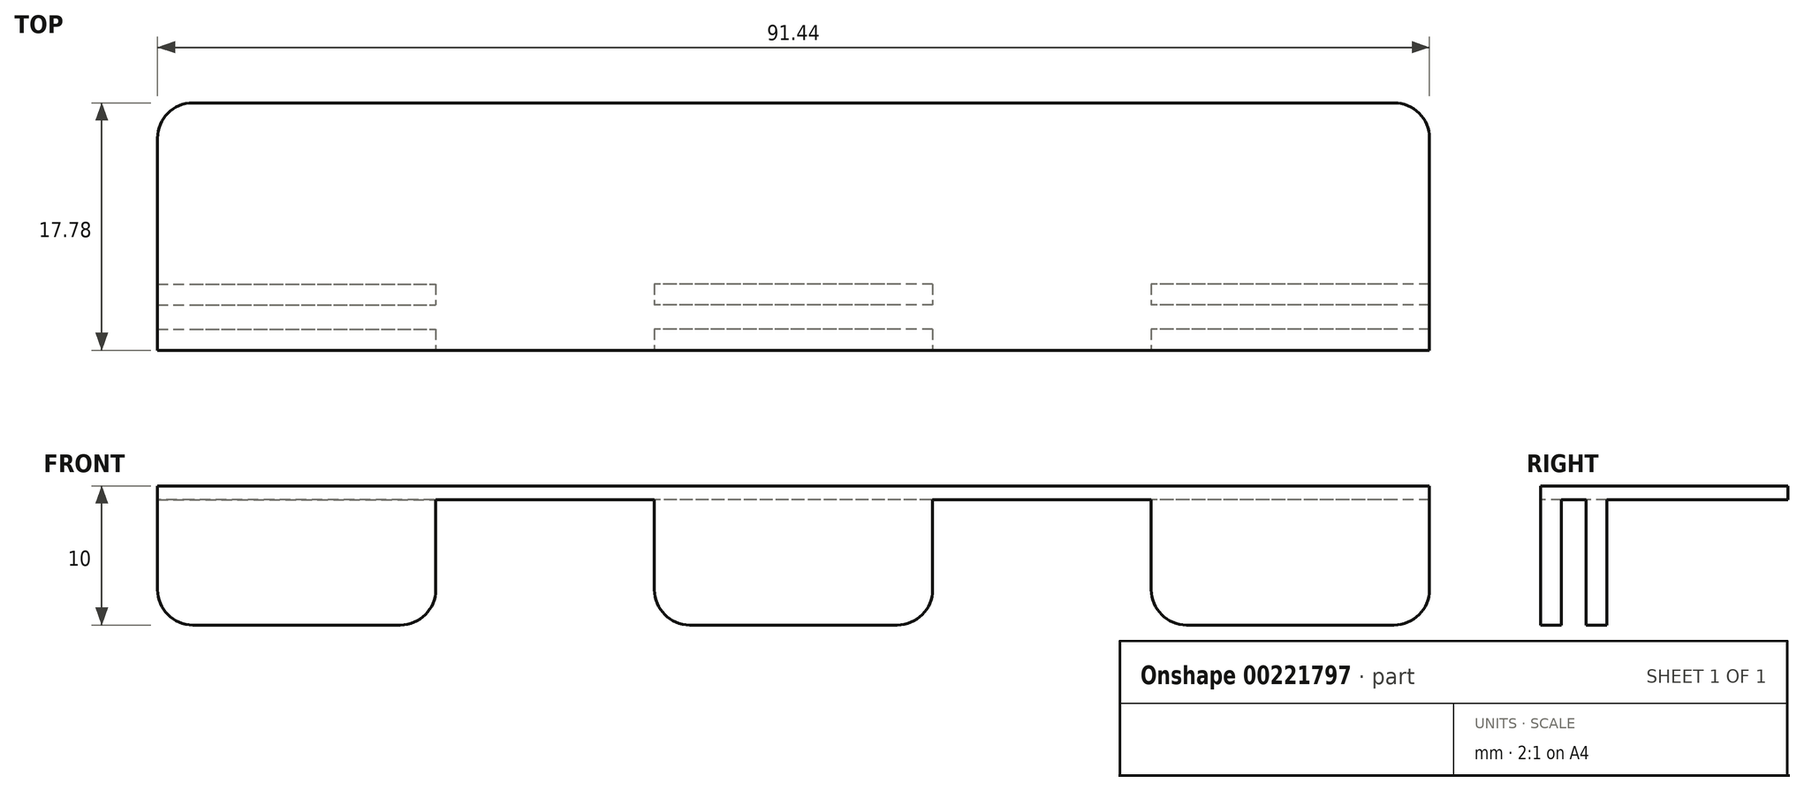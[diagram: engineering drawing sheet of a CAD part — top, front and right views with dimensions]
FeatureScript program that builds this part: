
annotation { "Feature Type Name" : "Feature", "Feature Type Description" : "" }
export const myFeature = defineFeature(function(context is Context, id is Id, definition is map)
    precondition{}
    {
        {
            var Q0;
            Q0=qCreatedBy(makeId("Top.planeOp"),FACE);
            var sketch = newSketch(context, id + "F0", { "sketchPlane" : qUnion([Q0])});
            skLineSegment(sketch, "E0", {"start": v(0, 0) * mm, "end": v(45.72, 0) * mm});
            skLineSegment(sketch, "E1", {"start": v(45.72, 0) * mm, "end": v(45.72, 17.78) * mm});
            skLineSegment(sketch, "E2", {"start": v(45.72, 17.78) * mm, "end": v(0, 17.78) * mm});
            skLineSegment(sketch, "E3", {"start": v(45.72, 3.25) * mm, "end": v(0, 3.25) * mm});
            skLineSegment(sketch, "E4", {"start": v(45.72, 4.75) * mm, "end": v(0, 4.75) * mm});
            skLineSegment(sketch, "E5", {"start": v(45.72, 1.5) * mm, "end": v(0, 1.5) * mm});
            skLineSegment(sketch, "E6.MirrorCS", {"start": v(-45.72, 17.78) * mm, "end": v(0, 17.78) * mm});
            skLineSegment(sketch, "E7.MirrorCS", {"start": v(-45.72, 4.75) * mm, "end": v(0, 4.75) * mm});
            skLineSegment(sketch, "E8.MirrorCS", {"start": v(-45.72, 3.25) * mm, "end": v(0, 3.25) * mm});
            skLineSegment(sketch, "E9.MirrorCS", {"start": v(-45.72, 1.5) * mm, "end": v(0, 1.5) * mm});
            skLineSegment(sketch, "E10.MirrorCS", {"start": v(0, 0) * mm, "end": v(-45.72, 0) * mm});
            skLineSegment(sketch, "E11.MirrorCS", {"start": v(-45.72, 0) * mm, "end": v(-45.72, 17.78) * mm});
            skLineSegment(sketch, "E12", {"start": v(25.72, 4.75) * mm, "end": v(25.72, 3.25) * mm});
            skLineSegment(sketch, "E13", {"start": v(25.72, 1.5) * mm, "end": v(25.72, 0) * mm});
            skLineSegment(sketch, "E14.MirrorCS", {"start": v(-25.72, 4.75) * mm, "end": v(-25.72, 3.25) * mm});
            skLineSegment(sketch, "E15.MirrorCS", {"start": v(-25.72, 1.5) * mm, "end": v(-25.72, 0) * mm});
            skLineSegment(sketch, "E16", {"start": v(10, 4.75) * mm, "end": v(10, 3.25) * mm});
            skLineSegment(sketch, "E17", {"start": v(10, 1.5) * mm, "end": v(10, 0) * mm});
            skLineSegment(sketch, "E18.MirrorCS", {"start": v(-10, 4.75) * mm, "end": v(-10, 3.25) * mm});
            skLineSegment(sketch, "E19.MirrorCS", {"start": v(-10, 1.5) * mm, "end": v(-10, 0) * mm});
            skSolve(sketch);
        }
        {
            var Q0;
            {var subQ1=sQuery(id+"F0.wireOp",EDGE,"E2");Q0=makeQuery(id+"F0.imprint","IMPRINT",FACE,{"disambiguationData":[TD([[makeQuery(id+"F0.imprint","IMPRINT",EDGE,{"derivedFrom":subQ1}),1.0]])]});}
            var Q1;
            {var subQ2=sQuery(id+"F0.wireOp",EDGE,"E3");Q1=makeQuery(id+"F0.imprint","IMPRINT",FACE,{"disambiguationData":[TD([[makeQuery(id+"F0.imprint","IMPRINT",EDGE,{"derivedFrom":subQ2}),-1.0]])]});}
            var Q2;
            {var subQ2=sQuery(id+"F0.wireOp",EDGE,"E3");Q2=makeQuery(id+"F0.imprint","IMPRINT",FACE,{"disambiguationData":[TD([[makeQuery(id+"F0.imprint","IMPRINT",EDGE,{"derivedFrom":subQ2}),1.0]])]});}
            var Q3;
            {var subQ2=sQuery(id+"F0.wireOp",EDGE,"E0");Q3=makeQuery(id+"F0.imprint","IMPRINT",FACE,{"disambiguationData":[TD([[makeQuery(id+"F0.imprint","IMPRINT",EDGE,{"derivedFrom":subQ2}),1.0]])]});}
            var Q4;
            {var subQ3=sQuery(id+"F0.wireOp",EDGE,"E14.MirrorCS");Q4=makeQuery(id+"F0.imprint","IMPRINT",FACE,{"disambiguationData":[TD([[makeQuery(id+"F0.imprint","IMPRINT",EDGE,{"derivedFrom":subQ3}),-1.0]])]});}
            var Q5;
            {var subQ3=sQuery(id+"F0.wireOp",EDGE,"E15.MirrorCS");Q5=makeQuery(id+"F0.imprint","IMPRINT",FACE,{"disambiguationData":[TD([[makeQuery(id+"F0.imprint","IMPRINT",EDGE,{"derivedFrom":subQ3}),-1.0]])]});}
            var Q6;
            {var subQ7=sQuery(id+"F0.wireOp",EDGE,"E12");Q6=makeQuery(id+"F0.imprint","IMPRINT",FACE,{"disambiguationData":[TD([[makeQuery(id+"F0.imprint","IMPRINT",EDGE,{"derivedFrom":subQ7}),-1.0]])]});}
            var Q7;
            {var subQ4=sQuery(id+"F0.wireOp",EDGE,"E13");Q7=makeQuery(id+"F0.imprint","IMPRINT",FACE,{"disambiguationData":[TD([[makeQuery(id+"F0.imprint","IMPRINT",EDGE,{"derivedFrom":subQ4}),-1.0]])]});}
            var Q8;
            {var subQ0=sQuery(id+"F0.wireOp",EDGE,"E15.MirrorCS");Q8=makeQuery(id+"F0.imprint","IMPRINT",FACE,{"disambiguationData":[TD([[makeQuery(id+"F0.imprint","IMPRINT",EDGE,{"derivedFrom":subQ0}),1.0]])]});}
            var Q9;
            {var subQ0=sQuery(id+"F0.wireOp",EDGE,"E14.MirrorCS");Q9=makeQuery(id+"F0.imprint","IMPRINT",FACE,{"disambiguationData":[TD([[makeQuery(id+"F0.imprint","IMPRINT",EDGE,{"derivedFrom":subQ0}),1.0]])]});}
            var Q10;
            {var subQ7=sQuery(id+"F0.wireOp",EDGE,"E16");Q10=makeQuery(id+"F0.imprint","IMPRINT",FACE,{"disambiguationData":[TD([[makeQuery(id+"F0.imprint","IMPRINT",EDGE,{"derivedFrom":subQ7}),-1.0]])]});}
            var Q11;
            {var subQ7=sQuery(id+"F0.wireOp",EDGE,"E17");Q11=makeQuery(id+"F0.imprint","IMPRINT",FACE,{"disambiguationData":[TD([[makeQuery(id+"F0.imprint","IMPRINT",EDGE,{"derivedFrom":subQ7}),-1.0]])]});}
            extrude(context, id + "F1", {"entities" : qUnion([Q0, Q1, Q2, Q3, Q4, Q5, Q6, Q7, Q8, Q9, Q10, Q11]), "depth" : 1 * mm, "offsetDistance" : 25 * mm});
        }
        {
            var Q0;
            {var subQ3=sQuery(id+"F0.wireOp",EDGE,"E13");Q0=makeQuery(id+"F0.imprint","IMPRINT",FACE,{"disambiguationData":[TD([[makeQuery(id+"F0.imprint","IMPRINT",EDGE,{"derivedFrom":subQ3}),1.0]])]});}
            var Q1;
            {var subQ5=sQuery(id+"F0.wireOp",EDGE,"E12");Q1=makeQuery(id+"F0.imprint","IMPRINT",FACE,{"disambiguationData":[TD([[makeQuery(id+"F0.imprint","IMPRINT",EDGE,{"derivedFrom":subQ5}),1.0]])]});}
            var Q2;
            {var subQ3=sQuery(id+"F0.wireOp",EDGE,"E14.MirrorCS");Q2=makeQuery(id+"F0.imprint","IMPRINT",FACE,{"disambiguationData":[TD([[makeQuery(id+"F0.imprint","IMPRINT",EDGE,{"derivedFrom":subQ3}),-1.0]])]});}
            var Q3;
            {var subQ3=sQuery(id+"F0.wireOp",EDGE,"E15.MirrorCS");Q3=makeQuery(id+"F0.imprint","IMPRINT",FACE,{"disambiguationData":[TD([[makeQuery(id+"F0.imprint","IMPRINT",EDGE,{"derivedFrom":subQ3}),-1.0]])]});}
            var Q4;
            {var subQ7=sQuery(id+"F0.wireOp",EDGE,"E16");Q4=makeQuery(id+"F0.imprint","IMPRINT",FACE,{"disambiguationData":[TD([[makeQuery(id+"F0.imprint","IMPRINT",EDGE,{"derivedFrom":subQ7}),-1.0]])]});}
            var Q5;
            {var subQ7=sQuery(id+"F0.wireOp",EDGE,"E17");Q5=makeQuery(id+"F0.imprint","IMPRINT",FACE,{"disambiguationData":[TD([[makeQuery(id+"F0.imprint","IMPRINT",EDGE,{"derivedFrom":subQ7}),-1.0]])]});}
            extrude(context, id + "F2", {"entities" : qUnion([Q0, Q1, Q2, Q3, Q4, Q5]), "operationType" : NewBodyOperationType.ADD, "oppositeDirection" : true, "depth" : 9 * mm, "offsetDistance" : 25 * mm});
        }
        {
            var Q0;
            Q0=makeQuery(id+"F1.opExtrude","SWEPT_EDGE",EDGE,{"disambiguationData":[OSD([sQuery(id+"F0.wireOp",EDGE,"E1"),sQuery(id+"F0.wireOp",EDGE,"E2")])]});
            var Q1;
            Q1=makeQuery(id+"F1.opExtrude","SWEPT_EDGE",EDGE,{"disambiguationData":[OSD([sQuery(id+"F0.wireOp",EDGE,"E6.MirrorCS"),sQuery(id+"F0.wireOp",EDGE,"E11.MirrorCS")])]});
            fillet(context, id + "F3", {"entities" : qUnion([Q0, Q1]), "radius" : 2.54 * mm, "tangentPropagation" : true, "allowEdgeOverflow" : false});
        }
        {
            var Q0;
            {var subQ0=sQuery(id+"F0.wireOp",EDGE,"E11.MirrorCS");Q0=makeQuery(id+"F2.opExtrude","CAP_EDGE",EDGE,{"disambiguationData":[OSD([subQ0]),TDD([makeQuery(id+"F0.imprint","IMPRINT",EDGE,{"disambiguationData":[TD([[makeQuery(id+"F0.imprint","INTERSECT",VERTEX,{"derivedFrom":[sQuery(id+"F0.wireOp",EDGE,"E9.MirrorCS"),subQ0]}),1.0]])],"derivedFrom":subQ0})])],"isStart":false});}
            var Q1;
            {var subQ0=sQuery(id+"F0.wireOp",EDGE,"E11.MirrorCS");Q1=makeQuery(id+"F2.opExtrude","CAP_EDGE",EDGE,{"disambiguationData":[OSD([subQ0]),TDD([makeQuery(id+"F0.imprint","IMPRINT",EDGE,{"disambiguationData":[TD([[makeQuery(id+"F0.imprint","INTERSECT",VERTEX,{"derivedFrom":[sQuery(id+"F0.wireOp",EDGE,"E7.MirrorCS"),subQ0]}),1.0]])],"derivedFrom":subQ0})])],"isStart":false});}
            var Q2;
            {var subQ0=sQuery(id+"F0.wireOp",EDGE,"E1");Q2=makeQuery(id+"F2.opExtrude","CAP_EDGE",EDGE,{"disambiguationData":[OSD([subQ0]),TDD([makeQuery(id+"F0.imprint","IMPRINT",EDGE,{"disambiguationData":[TD([[makeQuery(id+"F0.imprint","INTERSECT",VERTEX,{"derivedFrom":[sQuery(id+"F0.wireOp",EDGE,"E0"),subQ0]}),-1.0]])],"derivedFrom":subQ0})])],"isStart":false});}
            var Q3;
            {var subQ0=sQuery(id+"F0.wireOp",EDGE,"E1");Q3=makeQuery(id+"F2.opExtrude","CAP_EDGE",EDGE,{"disambiguationData":[OSD([subQ0]),TDD([makeQuery(id+"F0.imprint","IMPRINT",EDGE,{"disambiguationData":[TD([[makeQuery(id+"F0.imprint","INTERSECT",VERTEX,{"derivedFrom":[subQ0,sQuery(id+"F0.wireOp",EDGE,"E3")]}),-1.0]])],"derivedFrom":subQ0})])],"isStart":false});}
            var Q4;
            Q4=makeQuery(id+"F2.opExtrude","CAP_EDGE",EDGE,{"disambiguationData":[OSD([sQuery(id+"F0.wireOp",EDGE,"E15.MirrorCS")])],"isStart":false});
            var Q5;
            Q5=makeQuery(id+"F2.opExtrude","CAP_EDGE",EDGE,{"disambiguationData":[OSD([sQuery(id+"F0.wireOp",EDGE,"E14.MirrorCS")])],"isStart":false});
            var Q6;
            Q6=makeQuery(id+"F2.opExtrude","CAP_EDGE",EDGE,{"disambiguationData":[OSD([sQuery(id+"F0.wireOp",EDGE,"E18.MirrorCS")])],"isStart":false});
            var Q7;
            Q7=makeQuery(id+"F2.opExtrude","CAP_EDGE",EDGE,{"disambiguationData":[OSD([sQuery(id+"F0.wireOp",EDGE,"E19.MirrorCS")])],"isStart":false});
            var Q8;
            Q8=makeQuery(id+"F2.opExtrude","CAP_EDGE",EDGE,{"disambiguationData":[OSD([sQuery(id+"F0.wireOp",EDGE,"E17")])],"isStart":false});
            var Q9;
            Q9=makeQuery(id+"F2.opExtrude","CAP_EDGE",EDGE,{"disambiguationData":[OSD([sQuery(id+"F0.wireOp",EDGE,"E16")])],"isStart":false});
            var Q10;
            Q10=makeQuery(id+"F2.opExtrude","CAP_EDGE",EDGE,{"disambiguationData":[OSD([sQuery(id+"F0.wireOp",EDGE,"E12")])],"isStart":false});
            var Q11;
            Q11=makeQuery(id+"F2.opExtrude","CAP_EDGE",EDGE,{"disambiguationData":[OSD([sQuery(id+"F0.wireOp",EDGE,"E13")])],"isStart":false});
            fillet(context, id + "F4", {"entities" : qUnion([Q0, Q1, Q2, Q3, Q4, Q5, Q6, Q7, Q8, Q9, Q10, Q11]), "radius" : 2.54 * mm, "tangentPropagation" : true, "allowEdgeOverflow" : false});
        }
    });
